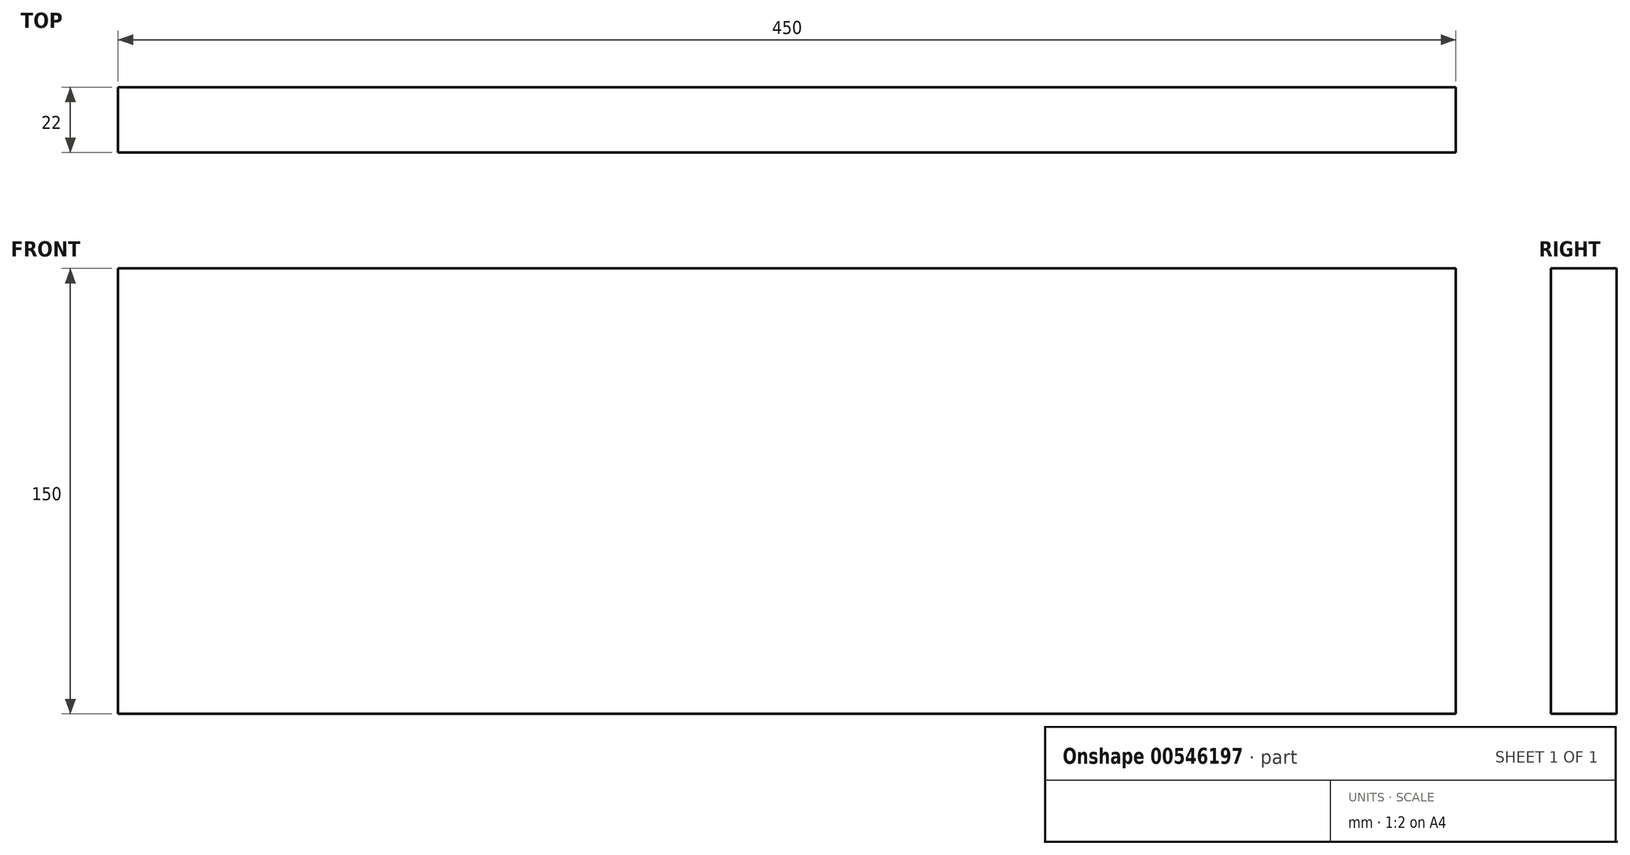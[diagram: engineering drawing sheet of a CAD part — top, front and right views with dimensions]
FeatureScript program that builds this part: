
annotation { "Feature Type Name" : "Feature", "Feature Type Description" : "" }
export const myFeature = defineFeature(function(context is Context, id is Id, definition is map)
    precondition{}
    {
        {
            var Q0;
            Q0=qCreatedBy(makeId("Front.planeOp"),FACE);
            var sketch = newSketch(context, id + "F0", { "sketchPlane" : qUnion([Q0])});
            skLineSegment(sketch, "E0.bottom", {"start": v(0, 0) * mm, "end": v(450, 0) * mm});
            skLineSegment(sketch, "E0.top", {"start": v(0, 150) * mm, "end": v(450, 150) * mm});
            skLineSegment(sketch, "E0.left", {"start": v(0, 0) * mm, "end": v(0, 150) * mm});
            skLineSegment(sketch, "E0.right", {"start": v(450, 0) * mm, "end": v(450, 150) * mm});
            skSolve(sketch);
        }
        {
            var Q0;
            Q0=makeQuery(id+"F0.imprint","IMPRINT",FACE,{"disambiguationData":[TD([[makeQuery(id+"F0.imprint","IMPRINT",EDGE,{"derivedFrom":sQuery(id+"F0.wireOp",EDGE,"E0.bottom")}),1.0]])]});
            extrude(context, id + "F1", {"entities" : qUnion([Q0]), "depth" : 22 * mm, "offsetDistance" : 25 * mm});
        }
    });
